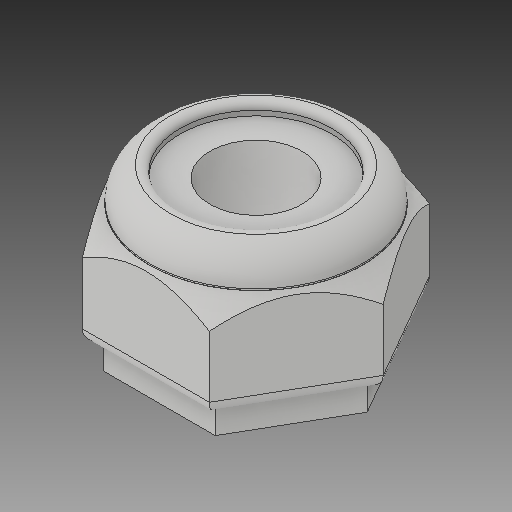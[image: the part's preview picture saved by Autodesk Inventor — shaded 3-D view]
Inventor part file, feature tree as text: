
AUTODESK INVENTOR PART (.ipt)
format: ipt  version: 2019.3 (Build 233278000, 278)  size: 168,960 bytes
history: native  units: in
note: dims shown in document units (in); Inventor stores cm internally (conversion verified against a paired STEP export)
features: extrude x1
ambient origin geometry x8: Origin, YZ Plane, XZ Plane, XY Plane, X Axis, Y Axis, Z Axis, Center Point
bodies: Solid1 (feature_tree)
feature tree (1):
  extrude  "Extrude1"  [1 undecoded]
note: 1 required parameter value undecoded (feature->parameter linkage not recoverable at this tier; creation-order binding heuristic only, values carry confidence <= 0.55)
